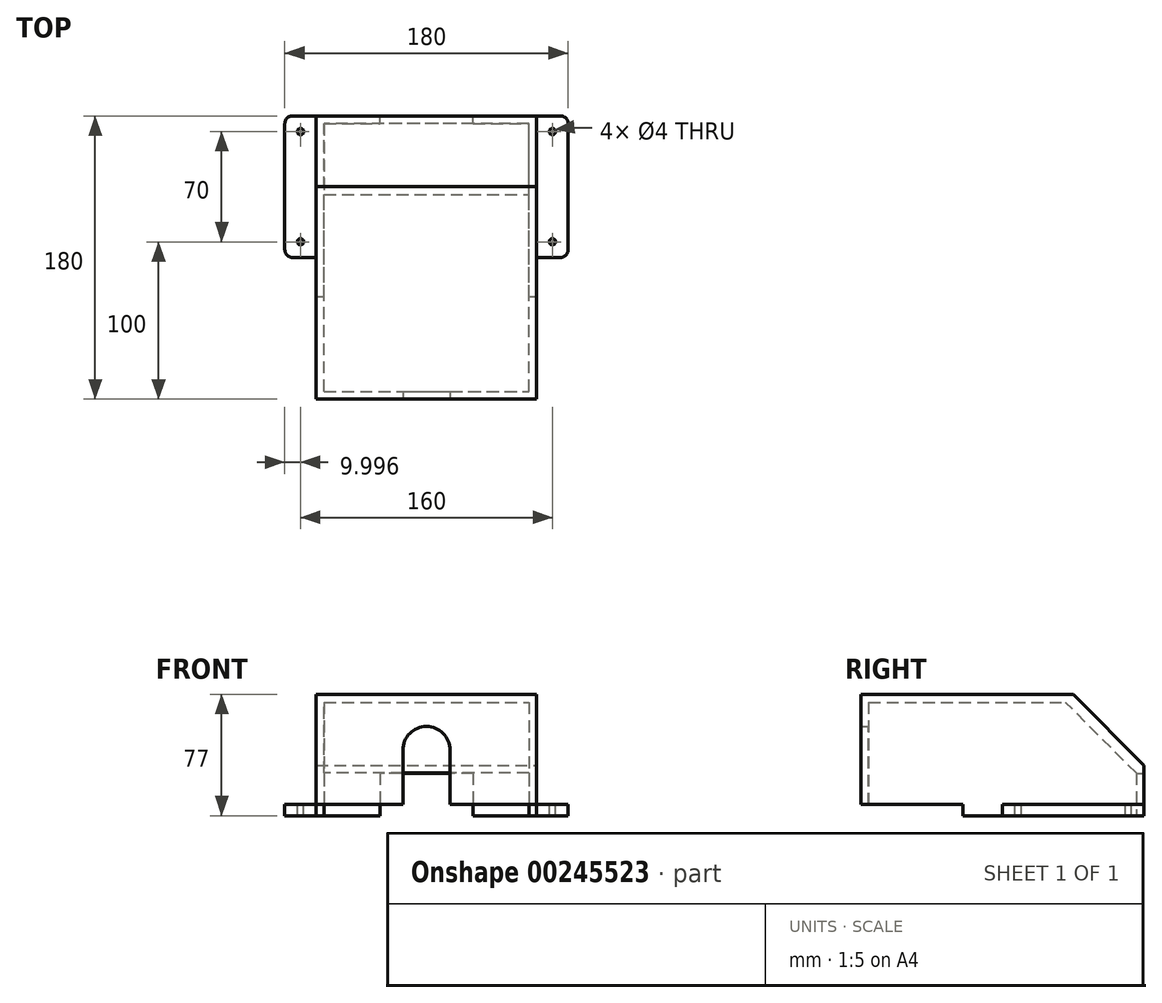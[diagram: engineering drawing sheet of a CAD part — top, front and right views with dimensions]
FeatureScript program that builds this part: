
annotation { "Feature Type Name" : "Feature", "Feature Type Description" : "" }
export const myFeature = defineFeature(function(context is Context, id is Id, definition is map)
    precondition{}
    {
        {
            var Q0;
            Q0=qCreatedBy(makeId("Top.planeOp"),FACE);
            var sketch = newSketch(context, id + "F0", { "sketchPlane" : qUnion([Q0])});
            skLineSegment(sketch, "E0.bottom", {"start": v(-23.4, 143.8) * mm, "end": v(116.6, 143.8) * mm});
            skLineSegment(sketch, "E0.top", {"start": v(-23.4, -36.2) * mm, "end": v(116.6, -36.2) * mm});
            skLineSegment(sketch, "E0.left", {"start": v(-23.4, 143.8) * mm, "end": v(-23.4, -36.2) * mm});
            skLineSegment(sketch, "E0.right", {"start": v(116.6, 143.8) * mm, "end": v(116.6, -36.2) * mm});
            skSolve(sketch);
        }
        {
            var Q0;
            Q0 = qSketchRegion(id + "F0", true);
            extrude(context, id + "F1", {"entities" : qUnion([Q0]), "depth" : 70 * mm});
        }
        {
            var Q0;
            Q0=makeQuery(id+"F1.opExtrude","CAP_FACE",FACE,{"disambiguationData":[OSD([sQuery(id+"F0.wireOp",EDGE,"E0.bottom"),sQuery(id+"F0.wireOp",EDGE,"E0.top"),sQuery(id+"F0.wireOp",EDGE,"E0.left"),sQuery(id+"F0.wireOp",EDGE,"E0.right")])],"isStart":true});
            var sketch = newSketch(context, id + "F2", { "sketchPlane" : qUnion([Q0])});
            skLineSegment(sketch, "E1.bottom", {"start": v(-18.4, 31.2) * mm, "end": v(111.6, 31.2) * mm});
            skLineSegment(sketch, "E1.top", {"start": v(-18.4, -138.8) * mm, "end": v(111.6, -138.8) * mm});
            skLineSegment(sketch, "E1.left", {"start": v(-18.4, 31.2) * mm, "end": v(-18.4, -138.8) * mm});
            skLineSegment(sketch, "E1.right", {"start": v(111.6, 31.2) * mm, "end": v(111.6, -138.8) * mm});
            skPoint(sketch, "E1.middle", {"position": v(46.6, -53.8) * mm});
            skPoint(sketch, "E1.middle.positionSnap0", {"position": v(-23.4, -53.8) * mm});
            skPoint(sketch, "E1.middle.positionSnap1", {"position": v(46.6, 36.2) * mm});
            skPoint(sketch, "E1.centerSnap0", {"position": v(-23.4, -53.8) * mm});
            skPoint(sketch, "E1.centerSnap1", {"position": v(46.6, 36.2) * mm});
            skSolve(sketch);
        }
        {
            var Q0;
            Q0=makeQuery(id+"F2.imprint","IMPRINT",FACE,{"disambiguationData":[TD([[makeQuery(id+"F2.imprint","IMPRINT",EDGE,{"derivedFrom":sQuery(id+"F2.wireOp",EDGE,"E1.bottom")}),-1.0]])]});
            extrude(context, id + "F3", {"entities" : qUnion([Q0]), "operationType" : NewBodyOperationType.REMOVE, "oppositeDirection" : true, "depth" : 65 * mm});
        }
        {
            var Q0;
            Q0=makeQuery(id+"F1.opExtrude","CAP_EDGE",EDGE,{"disambiguationData":[OSD([sQuery(id+"F0.wireOp",EDGE,"E0.bottom")])],"isStart":false});
            var Q1;
            Q1=makeQuery(id+"F3.boolean.opBoolean","COPY",EDGE,{"derivedFrom":makeQuery(id+"F3.opExtrude","CAP_EDGE",EDGE,{"disambiguationData":[OSD([sQuery(id+"F2.wireOp",EDGE,"E1.top")])],"isStart":false})});
            chamfer(context, id + "F4", {"entities" : qUnion([Q0, Q1]), "width" : 45 * mm, "tangentPropagation" : true});
        }
        {
            var Q0;
            Q0=makeQuery(id+"F1.opExtrude","SWEPT_FACE",FACE,{"disambiguationData":[OSD([sQuery(id+"F0.wireOp",EDGE,"E0.top")])]});
            var sketch = newSketch(context, id + "F5", { "sketchPlane" : qUnion([Q0])});
            skLineSegment(sketch, "E2.bottom", {"start": v(31.6, 49.63) * mm, "end": v(61.6, 49.63) * mm});
            skLineSegment(sketch, "E2.left", {"start": v(31.6, 49.63) * mm, "end": v(31.6, 0) * mm});
            skLineSegment(sketch, "E2.right", {"start": v(61.6, 49.63) * mm, "end": v(61.6, 0) * mm});
            skPoint(sketch, "E2.middle", {"position": v(46.6, 0) * mm});
            skLineSegment(sketch, "E3", {"start": v(31.6, 0) * mm, "end": v(61.6, 0) * mm});
            skSolve(sketch);
        }
        {
            var Q0;
            Q0=makeQuery(id+"F5.imprint","IMPRINT",FACE,{"disambiguationData":[TD([[makeQuery(id+"F5.imprint","IMPRINT",EDGE,{"derivedFrom":sQuery(id+"F5.wireOp",EDGE,"E2.bottom")}),-1.0]])]});
            extrude(context, id + "F6", {"entities" : qUnion([Q0]), "operationType" : NewBodyOperationType.REMOVE, "oppositeDirection" : true, "depth" : 25 * mm});
        }
        {
            var Q0;
            Q0=makeQuery(id+"F6.boolean.opBoolean","COPY",EDGE,{"derivedFrom":makeQuery(id+"F6.opExtrude","SWEPT_EDGE",EDGE,{"disambiguationData":[OSD([sQuery(id+"F5.wireOp",EDGE,"E2.bottom"),sQuery(id+"F5.wireOp",EDGE,"E2.right")])]})});
            var Q1;
            Q1=makeQuery(id+"F6.boolean.opBoolean","COPY",EDGE,{"derivedFrom":makeQuery(id+"F6.opExtrude","SWEPT_EDGE",EDGE,{"disambiguationData":[OSD([sQuery(id+"F5.wireOp",EDGE,"E2.bottom"),sQuery(id+"F5.wireOp",EDGE,"E2.left")])]})});
            fillet(context, id + "F7", {"entities" : qUnion([Q0, Q1]), "radius" : 15 * mm, "tangentPropagation" : true, "allowEdgeOverflow" : false});
        }
        {
            var Q0;
            Q0=makeQuery(id+"F1.opExtrude","CAP_FACE",FACE,{"disambiguationData":[OSD([sQuery(id+"F0.wireOp",EDGE,"E0.bottom"),sQuery(id+"F0.wireOp",EDGE,"E0.top"),sQuery(id+"F0.wireOp",EDGE,"E0.left"),sQuery(id+"F0.wireOp",EDGE,"E0.right")])],"isStart":true});
            var sketch = newSketch(context, id + "F8", { "sketchPlane" : qUnion([Q0])});
            skLineSegment(sketch, "E4", {"start": v(-23.4, -143.8) * mm, "end": v(-23.4, -28.8) * mm});
            skLineSegment(sketch, "E5", {"start": v(116.6, -143.8) * mm, "end": v(116.6, -28.8) * mm});
            skLineSegment(sketch, "E6", {"start": v(116.6, -28.8) * mm, "end": v(111.6, -28.8) * mm});
            skLineSegment(sketch, "E7", {"start": v(111.6, -28.8) * mm, "end": v(111.6, -138.8) * mm});
            skLineSegment(sketch, "E8", {"start": v(111.6, -138.8) * mm, "end": v(-18.4, -138.8) * mm});
            skLineSegment(sketch, "E9", {"start": v(-18.4, -138.8) * mm, "end": v(-18.4, -28.8) * mm});
            skLineSegment(sketch, "E10", {"start": v(-18.4, -28.8) * mm, "end": v(-23.4, -28.8) * mm});
            skLineSegment(sketch, "E11", {"start": v(-23.4, -143.8) * mm, "end": v(116.6, -143.8) * mm});
            skSolve(sketch);
        }
        {
            var Q0;
            Q0=makeQuery(id+"F8.imprint","IMPRINT",FACE,{"disambiguationData":[TD([[makeQuery(id+"F8.imprint","IMPRINT",EDGE,{"derivedFrom":sQuery(id+"F8.wireOp",EDGE,"E4")}),-1.0]])]});
            extrude(context, id + "F9", {"entities" : qUnion([Q0]), "operationType" : NewBodyOperationType.ADD, "depth" : 7 * mm});
        }
        {
            var Q0;
            Q0=makeQuery(id+"F9.boolean.opBoolean","MERGE",FACE,{"derivedFrom":[makeQuery(id+"F1.opExtrude","SWEPT_FACE",FACE,{"disambiguationData":[OSD([sQuery(id+"F0.wireOp",EDGE,"E0.bottom")])]}),makeQuery(id+"F9.opExtrude","SWEPT_FACE",FACE,{"disambiguationData":[OSD([sQuery(id+"F8.wireOp",EDGE,"E11")])]})]});
            var sketch = newSketch(context, id + "F10", { "sketchPlane" : qUnion([Q0])});
            skLineSegment(sketch, "E12.bottom", {"start": v(-76.2, 19.97) * mm, "end": v(-17, 19.97) * mm});
            skLineSegment(sketch, "E12.left", {"start": v(-76.2, 19.97) * mm, "end": v(-76.2, -7) * mm});
            skLineSegment(sketch, "E12.right", {"start": v(-17, 19.97) * mm, "end": v(-17, -7) * mm});
            skPoint(sketch, "E12.middle", {"position": v(-46.6, -7) * mm});
            skLineSegment(sketch, "E13", {"start": v(-76.2, -7) * mm, "end": v(-17, -7) * mm});
            skSolve(sketch);
        }
        {
            var Q0;
            Q0=makeQuery(id+"F10.imprint","IMPRINT",FACE,{"disambiguationData":[TD([[makeQuery(id+"F10.imprint","IMPRINT",EDGE,{"derivedFrom":sQuery(id+"F10.wireOp",EDGE,"E12.bottom")}),-1.0]])]});
            extrude(context, id + "F11", {"entities" : qUnion([Q0]), "operationType" : NewBodyOperationType.REMOVE, "oppositeDirection" : true, "depth" : 25 * mm});
        }
        {
            var Q0;
            Q0=makeQuery(id+"F9.boolean.opBoolean","MERGE",FACE,{"derivedFrom":[makeQuery(id+"F1.opExtrude","SWEPT_FACE",FACE,{"disambiguationData":[OSD([sQuery(id+"F0.wireOp",EDGE,"E0.left")])]}),makeQuery(id+"F9.opExtrude","SWEPT_FACE",FACE,{"disambiguationData":[OSD([sQuery(id+"F8.wireOp",EDGE,"E4")])]})]});
            var sketch = newSketch(context, id + "F12", { "sketchPlane" : qUnion([Q0])});
            skLineSegment(sketch, "E14.bottom", {"start": v(-143.8, -7) * mm, "end": v(-53.8, -7) * mm});
            skLineSegment(sketch, "E14.top", {"start": v(-143.8, 0) * mm, "end": v(-53.8, 0) * mm});
            skLineSegment(sketch, "E14.left", {"start": v(-143.8, -7) * mm, "end": v(-143.8, 0) * mm});
            skLineSegment(sketch, "E14.right", {"start": v(-53.8, -7) * mm, "end": v(-53.8, 0) * mm});
            skSolve(sketch);
        }
        {
            var Q0;
            Q0 = qSketchRegion(id + "F12", true);
            extrude(context, id + "F13", {"entities" : qUnion([Q0]), "operationType" : NewBodyOperationType.ADD, "depth" : 20 * mm});
        }
        {
            var Q0;
            Q0=makeQuery(id+"F9.boolean.opBoolean","MERGE",FACE,{"derivedFrom":[makeQuery(id+"F1.opExtrude","SWEPT_FACE",FACE,{"disambiguationData":[OSD([sQuery(id+"F0.wireOp",EDGE,"E0.right")])]}),makeQuery(id+"F9.opExtrude","SWEPT_FACE",FACE,{"disambiguationData":[OSD([sQuery(id+"F8.wireOp",EDGE,"E5")])]})]});
            var sketch = newSketch(context, id + "F14", { "sketchPlane" : qUnion([Q0])});
            skLineSegment(sketch, "E15.bottom", {"start": v(143.8, -7) * mm, "end": v(53.8, -7) * mm});
            skLineSegment(sketch, "E15.top", {"start": v(143.8, 0) * mm, "end": v(53.8, 0) * mm});
            skLineSegment(sketch, "E15.left", {"start": v(143.8, -7) * mm, "end": v(143.8, 0) * mm});
            skLineSegment(sketch, "E15.right", {"start": v(53.8, -7) * mm, "end": v(53.8, 0) * mm});
            skSolve(sketch);
        }
        {
            var Q0;
            Q0 = qSketchRegion(id + "F14", true);
            extrude(context, id + "F15", {"entities" : qUnion([Q0]), "operationType" : NewBodyOperationType.ADD, "depth" : 20 * mm});
        }
        {
            var Q0;
            Q0=makeQuery(id+"F13.opExtrude","SWEPT_FACE",FACE,{"disambiguationData":[OSD([sQuery(id+"F12.wireOp",EDGE,"E14.top")])]});
            var sketch = newSketch(context, id + "F16", { "sketchPlane" : qUnion([Q0])});
            skLineSegment(sketch, "E16", {"start": v(-33.4, 143.8) * mm, "end": v(-33.4, 133.8) * mm});
            skLineSegment(sketch, "E17", {"start": v(-33.4, 53.8) * mm, "end": v(-33.4, 63.8) * mm});
            skCircle(sketch, "E18", {"center": v(-33.4, 133.8) * mm, "radius": 2 * mm});
            skCircle(sketch, "E19", {"center": v(-33.4, 63.8) * mm, "radius": 2 * mm});
            skSolve(sketch);
        }
        {
            var Q0;
            Q0 = qSketchRegion(id + "F16", true);
            extrude(context, id + "F17", {"entities" : qUnion([Q0]), "operationType" : NewBodyOperationType.REMOVE, "oppositeDirection" : true, "depth" : 25 * mm});
        }
        {
            var Q0;
            Q0=makeQuery(id+"F15.opExtrude","SWEPT_FACE",FACE,{"disambiguationData":[OSD([sQuery(id+"F14.wireOp",EDGE,"E15.top")])]});
            var sketch = newSketch(context, id + "F18", { "sketchPlane" : qUnion([Q0])});
            skLineSegment(sketch, "E20", {"start": v(126.6, 143.8) * mm, "end": v(126.6, 133.8) * mm});
            skLineSegment(sketch, "E21", {"start": v(126.6, 53.8) * mm, "end": v(126.6, 63.8) * mm});
            skCircle(sketch, "E22", {"center": v(126.6, 63.8) * mm, "radius": 2 * mm});
            skCircle(sketch, "E23", {"center": v(126.6, 133.8) * mm, "radius": 2 * mm});
            skSolve(sketch);
        }
        {
            var Q0;
            Q0 = qSketchRegion(id + "F18", true);
            extrude(context, id + "F19", {"entities" : qUnion([Q0]), "operationType" : NewBodyOperationType.REMOVE, "oppositeDirection" : true, "depth" : 25 * mm});
        }
        {
            var Q0;
            Q0=makeQuery(id+"F13.opExtrude","CAP_EDGE",EDGE,{"disambiguationData":[OSD([sQuery(id+"F12.wireOp",EDGE,"E14.right")])],"isStart":false});
            var Q1;
            Q1=makeQuery(id+"F13.opExtrude","CAP_EDGE",EDGE,{"disambiguationData":[OSD([sQuery(id+"F12.wireOp",EDGE,"E14.left")])],"isStart":false});
            var Q2;
            Q2=makeQuery(id+"F15.opExtrude","CAP_EDGE",EDGE,{"disambiguationData":[OSD([sQuery(id+"F14.wireOp",EDGE,"E15.left")])],"isStart":false});
            var Q3;
            Q3=makeQuery(id+"F15.opExtrude","CAP_EDGE",EDGE,{"disambiguationData":[OSD([sQuery(id+"F14.wireOp",EDGE,"E15.right")])],"isStart":false});
            fillet(context, id + "F20", {"entities" : qUnion([Q0, Q1, Q2, Q3]), "radius" : 5 * mm, "tangentPropagation" : true, "allowEdgeOverflow" : false});
        }
    });
